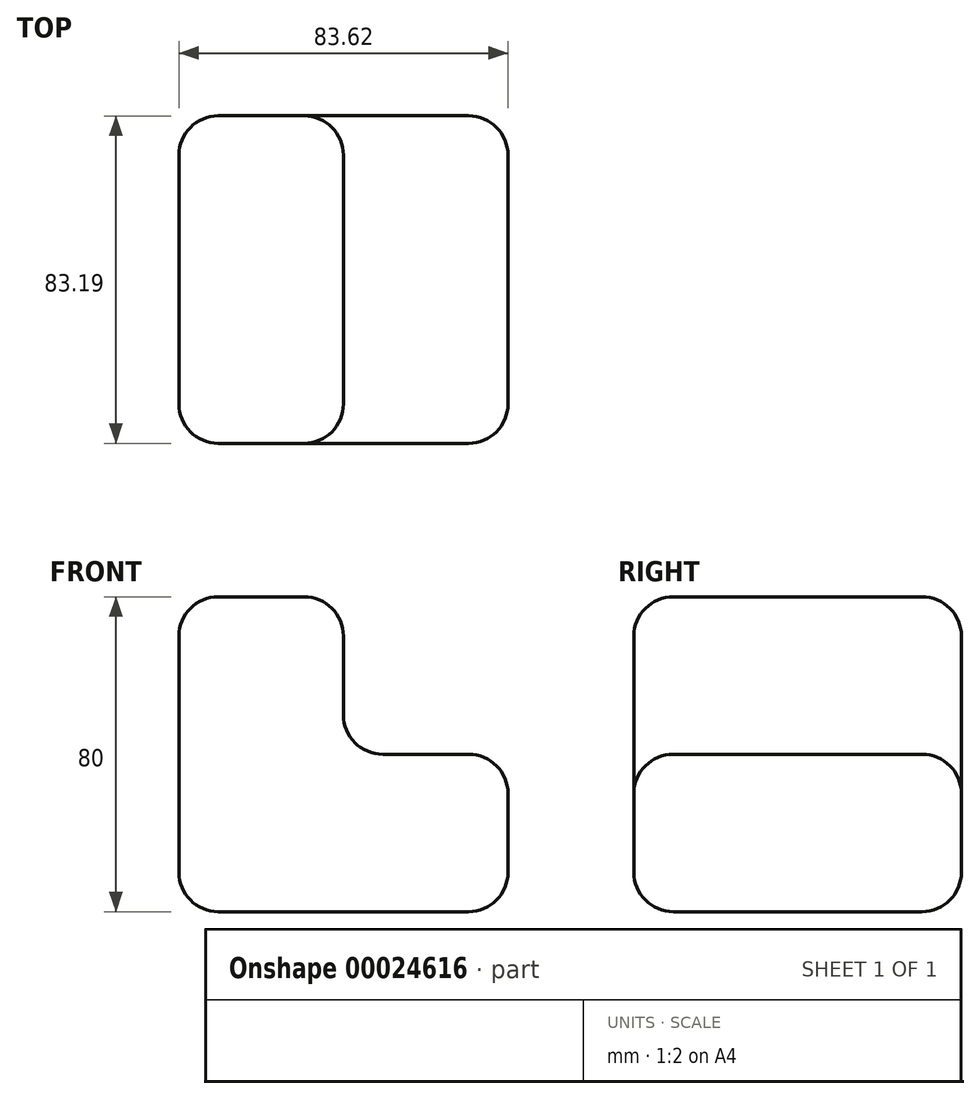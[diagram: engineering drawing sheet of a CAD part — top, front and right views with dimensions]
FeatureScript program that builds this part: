
annotation { "Feature Type Name" : "Feature", "Feature Type Description" : "" }
export const myFeature = defineFeature(function(context is Context, id is Id, definition is map)
    precondition{}
    {
        {
            var Q0;
            Q0=qCreatedBy(makeId("Top.planeOp"),FACE);
            var sketch = newSketch(context, id + "F0", { "sketchPlane" : qUnion([Q0])});
            skLineSegment(sketch, "E0.bottom", {"start": v(-59.13, -45.93) * mm, "end": v(24.5, -45.93) * mm});
            skLineSegment(sketch, "E0.top", {"start": v(-59.13, 37.26) * mm, "end": v(24.5, 37.26) * mm});
            skLineSegment(sketch, "E0.left", {"start": v(-59.13, -45.93) * mm, "end": v(-59.13, 37.26) * mm});
            skLineSegment(sketch, "E0.right", {"start": v(24.5, -45.93) * mm, "end": v(24.5, 37.26) * mm});
            skSolve(sketch);
        }
        {
            var Q0;
            Q0=makeQuery(id+"F0.imprint","IMPRINT",FACE,{"disambiguationData":[TD([[makeQuery(id+"F0.imprint","IMPRINT",EDGE,{"derivedFrom":sQuery(id+"F0.wireOp",EDGE,"E0.bottom")}),1.0]])]});
            extrude(context, id + "F1", {"entities" : qUnion([Q0]), "depth" : 40 * mm});
        }
        {
            var Q0;
            Q0=makeQuery(id+"F1.opExtrude","CAP_FACE",FACE,{"disambiguationData":[OSD([sQuery(id+"F0.wireOp",EDGE,"E0.bottom"),sQuery(id+"F0.wireOp",EDGE,"E0.top"),sQuery(id+"F0.wireOp",EDGE,"E0.left"),sQuery(id+"F0.wireOp",EDGE,"E0.right")])],"isStart":false});
            var sketch = newSketch(context, id + "F2", { "sketchPlane" : qUnion([Q0])});
            skLineSegment(sketch, "E1", {"start": v(-17.32, 37.26) * mm, "end": v(-17.32, -45.93) * mm});
            skSolve(sketch);
        }
        {
            var Q0;
            {var subQ1=sQuery(id+"F2.wireOp",EDGE,"E1");Q0=makeQuery(id+"F2.imprint","IMPRINT",FACE,{"disambiguationData":[TD([[makeQuery(id+"F2.imprint","IMPRINT",EDGE,{"derivedFrom":subQ1}),-1.0]])]});}
            extrude(context, id + "F3", {"entities" : qUnion([Q0]), "operationType" : NewBodyOperationType.ADD, "depth" : 40 * mm});
        }
        {
            var Q0;
            Q0=makeQuery(id+"F3.opExtrude","CAP_EDGE",EDGE,{"disambiguationData":[OSD([sQuery(id+"F0.wireOp",EDGE,"E0.bottom")])],"isStart":false});
            var Q1;
            Q1=makeQuery(id+"F3.opExtrude","CAP_EDGE",EDGE,{"disambiguationData":[OSD([sQuery(id+"F2.wireOp",EDGE,"E1")])],"isStart":false});
            var Q2;
            Q2=makeQuery(id+"F3.opExtrude","SWEPT_EDGE",EDGE,{"disambiguationData":[OSD([sQuery(id+"F0.wireOp",EDGE,"E0.bottom"),sQuery(id+"F2.wireOp",EDGE,"E1")])]});
            var Q3;
            Q3=makeQuery(id+"F1.opExtrude","CAP_EDGE",EDGE,{"disambiguationData":[OSD([sQuery(id+"F0.wireOp",EDGE,"E0.bottom")])],"isStart":false});
            var Q4;
            Q4=makeQuery(id+"F1.opExtrude","CAP_EDGE",EDGE,{"disambiguationData":[OSD([sQuery(id+"F0.wireOp",EDGE,"E0.right")])],"isStart":false});
            var Q5;
            {var subQ0=sQuery(id+"F0.wireOp",EDGE,"E0.bottom");Q5=makeQuery(id+"F3.boolean.opBoolean","MERGE",FACE,{"derivedFrom":[makeQuery(id+"F1.opExtrude","SWEPT_FACE",FACE,{"disambiguationData":[OSD([subQ0])]}),makeQuery(id+"F3.opExtrude","SWEPT_FACE",FACE,{"disambiguationData":[OSD([subQ0])]})]});}
            var Q6;
            Q6=makeQuery(id+"F1.opExtrude","SWEPT_FACE",FACE,{"disambiguationData":[OSD([sQuery(id+"F0.wireOp",EDGE,"E0.right")])]});
            var Q7;
            Q7=makeQuery(id+"F3.opExtrude","SWEPT_FACE",FACE,{"disambiguationData":[OSD([sQuery(id+"F2.wireOp",EDGE,"E1")])]});
            var Q8;
            Q8=makeQuery(id+"F1.opExtrude","CAP_FACE",FACE,{"disambiguationData":[OSD([sQuery(id+"F0.wireOp",EDGE,"E0.bottom"),sQuery(id+"F0.wireOp",EDGE,"E0.top"),sQuery(id+"F0.wireOp",EDGE,"E0.left"),sQuery(id+"F0.wireOp",EDGE,"E0.right")])],"isStart":false});
            var Q9;
            Q9=makeQuery(id+"F3.opExtrude","CAP_FACE",FACE,{"disambiguationData":[OSD([sQuery(id+"F0.wireOp",EDGE,"E0.bottom"),sQuery(id+"F0.wireOp",EDGE,"E0.top"),sQuery(id+"F0.wireOp",EDGE,"E0.left"),sQuery(id+"F2.wireOp",EDGE,"E1")])],"isStart":false});
            fillet(context, id + "F4", {"entities" : qUnion([Q0, Q1, Q2, Q3, Q4, Q5, Q6, Q7, Q8, Q9]), "radius" : 10 * mm, "tangentPropagation" : true, "allowEdgeOverflow" : false});
        }
        {
            var Q0;
            {var subQ0=sQuery(id+"F0.wireOp",EDGE,"E0.left");Q0=makeQuery(id+"F3.boolean.opBoolean","MERGE",FACE,{"derivedFrom":[makeQuery(id+"F1.opExtrude","SWEPT_FACE",FACE,{"disambiguationData":[OSD([subQ0])]}),makeQuery(id+"F3.opExtrude","SWEPT_FACE",FACE,{"disambiguationData":[OSD([subQ0])]})]});}
            var Q1;
            {var subQ0=sQuery(id+"F0.wireOp",EDGE,"E0.top");Q1=makeQuery(id+"F3.boolean.opBoolean","MERGE",FACE,{"derivedFrom":[makeQuery(id+"F1.opExtrude","SWEPT_FACE",FACE,{"disambiguationData":[OSD([subQ0])]}),makeQuery(id+"F3.opExtrude","SWEPT_FACE",FACE,{"disambiguationData":[OSD([subQ0])]})]});}
            fillet(context, id + "F5", {"entities" : qUnion([Q0, Q1]), "radius" : 10 * mm, "tangentPropagation" : true, "allowEdgeOverflow" : false});
        }
    });
